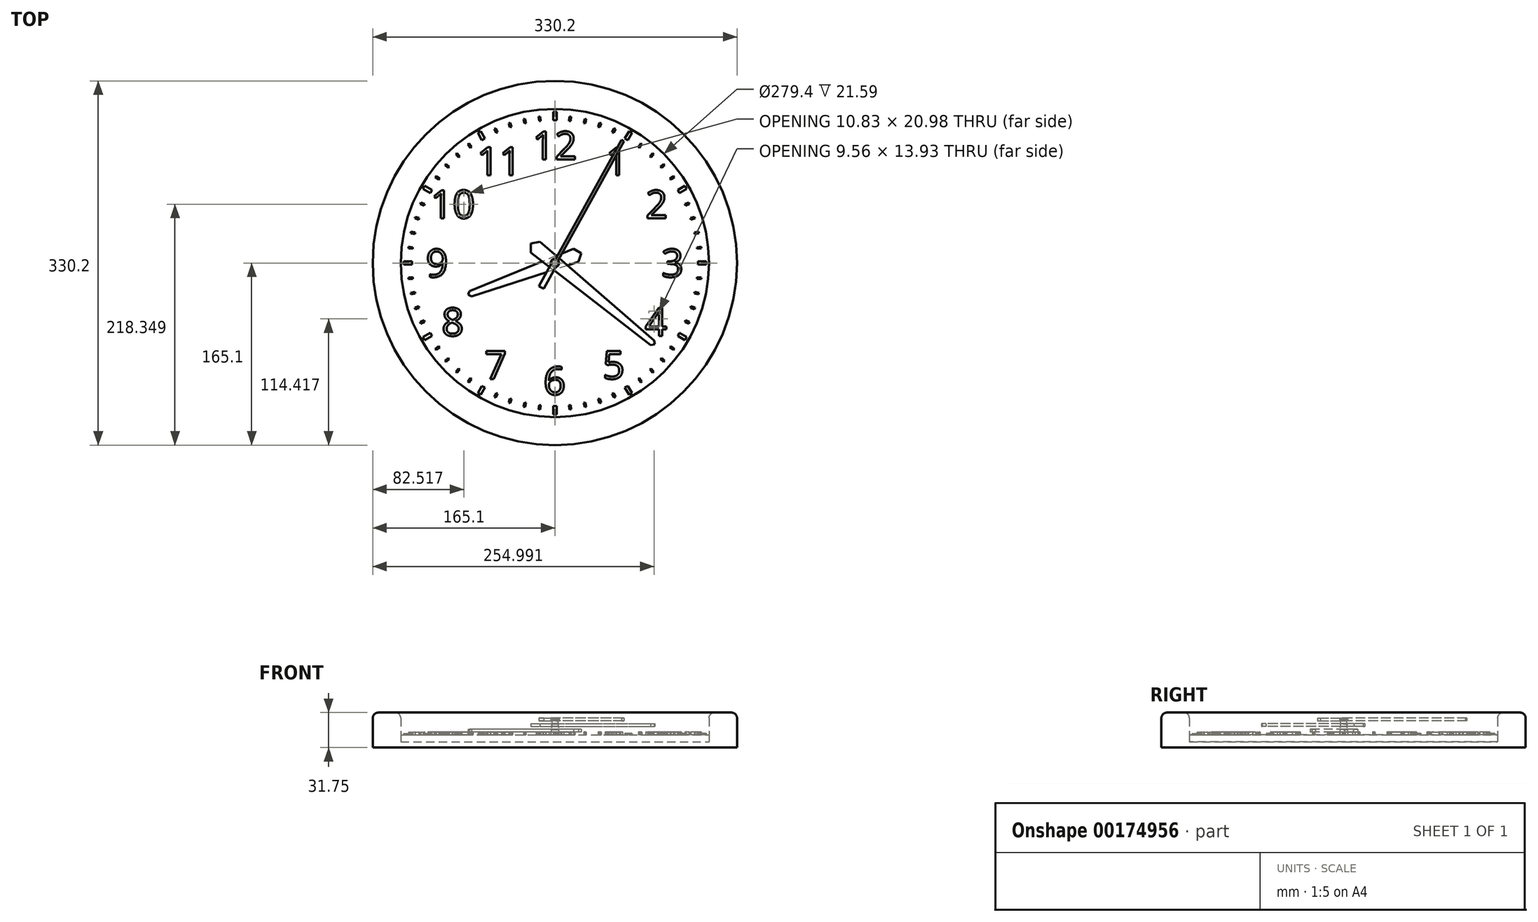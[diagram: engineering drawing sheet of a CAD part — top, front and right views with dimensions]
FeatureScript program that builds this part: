
annotation { "Feature Type Name" : "Feature", "Feature Type Description" : "" }
export const myFeature = defineFeature(function(context is Context, id is Id, definition is map)
    precondition{}
    {
        {
            var Q0;
            Q0=qCreatedBy(makeId("Front.planeOp"),FACE);
            var sketch = newSketch(context, id + "F0", { "sketchPlane" : qUnion([Q0])});
            skLineSegment(sketch, "E0", {"start": v(0, 0) * mm, "end": v(0, 54.8) * mm, "construction": true});
            skLineSegment(sketch, "E1.bottom", {"start": v(139.7, 0) * mm, "end": v(165.1, 0) * mm});
            skLineSegment(sketch, "E1.top", {"start": v(139.7, 31.75) * mm, "end": v(165.1, 31.75) * mm});
            skLineSegment(sketch, "E1.left", {"start": v(139.7, 5.08) * mm, "end": v(139.7, 31.75) * mm});
            skLineSegment(sketch, "E1.right", {"start": v(165.1, 0) * mm, "end": v(165.1, 31.75) * mm});
            skLineSegment(sketch, "E2", {"start": v(152.4, 0) * mm, "end": v(152.4, 31.75) * mm, "construction": true});
            skLineSegment(sketch, "E3.bottom", {"start": v(0, 0) * mm, "end": v(139.7, 0) * mm});
            skLineSegment(sketch, "E3.top", {"start": v(0, 5.08) * mm, "end": v(139.7, 5.08) * mm});
            skLineSegment(sketch, "E3.left", {"start": v(0, 0) * mm, "end": v(0, 5.08) * mm});
            skSolve(sketch);
        }
        {
            var Q0;
            Q0=makeQuery(id+"F0.imprint","IMPRINT",FACE,{"disambiguationData":[TD([[makeQuery(id+"F0.imprint","IMPRINT",EDGE,{"derivedFrom":sQuery(id+"F0.wireOp",EDGE,"E1.bottom")}),1.0]])]});
            var Q1;
            Q1=sQuery(id+"F0.wireOp",EDGE,"E0");
            revolve(context, id + "F1", {"entities" : qUnion([Q0]), "axis" : qUnion([Q1]), "revolveType" : RevolveType.FULL});
        }
        {
            var Q0;
            Q0=makeQuery(id+"F1.opRevolve","SWEPT_EDGE",EDGE,{"disambiguationData":[OSD([sQuery(id+"F0.wireOp",EDGE,"E1.top"),sQuery(id+"F0.wireOp",EDGE,"E1.left")])]});
            var Q1;
            Q1=makeQuery(id+"F1.opRevolve","SWEPT_EDGE",EDGE,{"disambiguationData":[OSD([sQuery(id+"F0.wireOp",EDGE,"E1.top"),sQuery(id+"F0.wireOp",EDGE,"E1.right")])]});
            fillet(context, id + "F2", {"entities" : qUnion([Q0, Q1]), "radius" : 5.08 * mm, "tangentPropagation" : true, "allowEdgeOverflow" : false});
        }
        {
            var Q0;
            Q0=makeQuery(id+"F1.opRevolve","SWEPT_FACE",FACE,{"disambiguationData":[OSD([sQuery(id+"F0.wireOp",EDGE,"E3.top")])]});
            extrude(context, id + "F3", {"entities" : qUnion([Q0]), "depth" : 6.35 * mm});
        }
        {
            var Q0;
            Q0=makeQuery(id+"F3.opExtrude","CAP_FACE",FACE,{"disambiguationData":[OSD([sQuery(id+"F0.wireOp",EDGE,"E3.top")])],"isStart":false});
            var sketch = newSketch(context, id + "F4", { "sketchPlane" : qUnion([Q0])});
            skText(sketch, "E4", { "text": "12", "fontName": "OpenSans-Regular.ttf"});
            skLineSegment(sketch, "E5", {"start": v(0, 0) * mm, "end": v(0, 106.68) * mm, "construction": true});
            skLineSegment(sketch, "E6.1.0", {"start": v(0, 0) * mm, "end": v(-53.34, 92.39) * mm, "construction": true});
            skLineSegment(sketch, "E6.2.0", {"start": v(0, 0) * mm, "end": v(-92.39, 53.34) * mm, "construction": true});
            skLineSegment(sketch, "E6.3.0", {"start": v(0, 0) * mm, "end": v(-106.68, 0) * mm, "construction": true});
            skLineSegment(sketch, "E6.4.0", {"start": v(0, 0) * mm, "end": v(-92.39, -53.34) * mm, "construction": true});
            skLineSegment(sketch, "E6.5.0", {"start": v(0, 0) * mm, "end": v(-53.34, -92.39) * mm, "construction": true});
            skLineSegment(sketch, "E6.6.0", {"start": v(0, 0) * mm, "end": v(0, -106.68) * mm, "construction": true});
            skLineSegment(sketch, "E6.7.0", {"start": v(0, 0) * mm, "end": v(53.34, -92.39) * mm, "construction": true});
            skLineSegment(sketch, "E6.8.0", {"start": v(0, 0) * mm, "end": v(92.39, -53.34) * mm, "construction": true});
            skLineSegment(sketch, "E6.9.0", {"start": v(0, 0) * mm, "end": v(106.68, 0) * mm, "construction": true});
            skLineSegment(sketch, "E6.10.0", {"start": v(0, 0) * mm, "end": v(92.39, 53.34) * mm, "construction": true});
            skLineSegment(sketch, "E6.11.0", {"start": v(0, 0) * mm, "end": v(53.34, 92.39) * mm, "construction": true});
            skPoint(sketch, "E6.center", {"position": v(0, 0) * mm});
            skText(sketch, "E7", { "text": "2", "fontName": "OpenSans-Regular.ttf"});
            skText(sketch, "E8", { "text": "3", "fontName": "OpenSans-Regular.ttf"});
            skText(sketch, "E9", { "text": "4", "fontName": "OpenSans-Regular.ttf"});
            skText(sketch, "E10", { "text": "1", "fontName": "OpenSans-Regular.ttf"});
            skText(sketch, "E11", { "text": "5", "fontName": "OpenSans-Regular.ttf"});
            skText(sketch, "E12", { "text": "6", "fontName": "OpenSans-Regular.ttf"});
            skText(sketch, "E13", { "text": "7", "fontName": "OpenSans-Regular.ttf"});
            skText(sketch, "E14", { "text": "9", "fontName": "OpenSans-Regular.ttf"});
            skText(sketch, "E15", { "text": "8", "fontName": "OpenSans-Regular.ttf"});
            skText(sketch, "E16", { "text": "10", "fontName": "OpenSans-Regular.ttf"});
            skText(sketch, "E17", { "text": "11", "fontName": "OpenSans-Regular.ttf"});
            const initialGuessF4  = {"E4": [-0.02037, 0.09398, 1, 0, 0.0254], "E7": [0.0821, 0.04064, 1, 0, 0.0254], "E8": [0.09649, -0.0127, 1, 0, 0.0254], "E9": [0.08151, -0.06604, 1, 0, 0.0254], "E10": [0.04604, 0.07969, 1, 0, 0.0254], "E11": [0.04313, -0.10509, 1, 0, 0.0254], "E12": [-0.01037, -0.11938, 1, 0, 0.0254], "E13": [-0.06367, -0.10509, 1, 0, 0.0254], "E14": [-0.11696, -0.0127, 1, 0, 0.0254], "E15": [-0.1027, -0.06604, 1, 0, 0.0254], "E16": [-0.11282, 0.04064, 1, 0, 0.0254], "E17": [-0.07073, 0.07969, 1, 0, 0.0254]};
            skSetInitialGuess(sketch, initialGuessF4);
            skSolve(sketch);
        }
        {
            var Q0;
            Q0 = qSketchRegion(id + "F4", true);
            extrude(context, id + "F5", {"entities" : qUnion([Q0]), "depth" : 2.54 * mm});
        }
        {
            var Q0;
            Q0=makeQuery(id+"F3.opExtrude","CAP_FACE",FACE,{"disambiguationData":[OSD([sQuery(id+"F0.wireOp",EDGE,"E3.top")])],"isStart":false});
            var sketch = newSketch(context, id + "F6", { "sketchPlane" : qUnion([Q0])});
            skCircle(sketch, "E18", {"center": v(0, 0) * mm, "radius": 3.81 * mm});
            skSolve(sketch);
        }
        {
            var Q0;
            Q0=makeQuery(id+"F6.imprint","IMPRINT",FACE,{"disambiguationData":[TD([[makeQuery(id+"F6.imprint","IMPRINT",EDGE,{"derivedFrom":sQuery(id+"F6.wireOp",EDGE,"E18")}),-1.0]])]});
            cPlane(context, id + "F7", {"entities" : qUnion([Q0]), "cplaneType" : CPlaneType.OFFSET, "offset" : 13.97 * mm, "width" : 152.4 * mm, "height" : 152.4 * mm});
        }
        {
            var Q0;
            Q0=qCreatedBy(id+"F7.planeOp",FACE);
            var sketch = newSketch(context, id + "F8", { "sketchPlane" : qUnion([Q0])});
            skCircle(sketch, "E19", {"center": v(0, 0) * mm, "radius": 2.54 * mm});
            skSolve(sketch);
        }
        {
            var Q1;
            Q1=makeQuery(id+"F6.imprint","IMPRINT",FACE,{"disambiguationData":[TD([[makeQuery(id+"F6.imprint","IMPRINT",EDGE,{"derivedFrom":sQuery(id+"F6.wireOp",EDGE,"E18")}),1.0]])]});
            var Q2;
            Q2=makeQuery(id+"F8.imprint","IMPRINT",FACE,{"disambiguationData":[TD([[makeQuery(id+"F8.imprint","IMPRINT",EDGE,{"derivedFrom":sQuery(id+"F8.wireOp",EDGE,"E19")}),1.0]])]});
            loft(context, id + "F9", {"sheetProfilesArray" : [{ "sheetProfileEntities" : qUnion([Q1]) }, { "sheetProfileEntities" : qUnion([Q2]) }]});
        }
        {
            var Q0;
            Q0=makeQuery(id+"F3.opExtrude","CAP_FACE",FACE,{"disambiguationData":[OSD([sQuery(id+"F0.wireOp",EDGE,"E3.top")])],"isStart":false});
            cPlane(context, id + "F10", {"entities" : qUnion([Q0]), "cplaneType" : CPlaneType.OFFSET, "offset" : 2.54 * mm, "width" : 152.4 * mm, "height" : 152.4 * mm});
        }
        {
            var Q0;
            Q0=qCreatedBy(id+"F10.planeOp",FACE);
            var sketch = newSketch(context, id + "F11", { "sketchPlane" : qUnion([Q0])});
            skLineSegment(sketch, "E20", {"start": v(-4.77, -1.74) * mm, "end": v(-76.38, -27.8) * mm, "construction": true});
            skLineSegment(sketch, "E21", {"start": v(-76.38, -27.8) * mm, "end": v(-77.25, -25.41) * mm, "construction": true});
            skLineSegment(sketch, "E22", {"start": v(19.1, 6.95) * mm, "end": v(16.92, 12.92) * mm, "construction": true});
            skLineSegment(sketch, "E23", {"start": v(-4.77, -1.74) * mm, "end": v(23.87, 8.69) * mm, "construction": true});
            skLineSegment(sketch, "E24", {"start": v(23.87, 8.69) * mm, "end": v(16.92, 12.92) * mm});
            skLineSegment(sketch, "E25", {"start": v(16.92, 12.92) * mm, "end": v(-77.25, -25.41) * mm});
            skLineSegment(sketch, "E26", {"start": v(-76.38, -27.8) * mm, "end": v(-78.77, -28.67) * mm, "construction": true});
            skLineSegment(sketch, "E27", {"start": v(-78.77, -28.67) * mm, "end": v(-77.25, -25.41) * mm});
            skLineSegment(sketch, "E28.MirrorCS", {"start": v(-78.77, -28.67) * mm, "end": v(-75.5, -30.19) * mm});
            skLineSegment(sketch, "E29.MirrorCS", {"start": v(21.27, 0.98) * mm, "end": v(-75.5, -30.19) * mm});
            skLineSegment(sketch, "E30.MirrorCS", {"start": v(23.87, 8.69) * mm, "end": v(21.27, 0.98) * mm});
            skSolve(sketch);
        }
        {
            var Q0;
            Q0=makeQuery(id+"F11.imprint","IMPRINT",FACE,{"disambiguationData":[TD([[makeQuery(id+"F11.imprint","IMPRINT",EDGE,{"derivedFrom":sQuery(id+"F11.wireOp",EDGE,"E24")}),1.0]])]});
            var Q1;
            Q1=makeQuery(id+"F11.imprint","IMPRINT",FACE,{"disambiguationData":[TD([[makeQuery(id+"F11.imprint","IMPRINT",EDGE,{"derivedFrom":makeQuery(id+"F9.opLoft","MID_CAP_EDGE",EDGE,{"disambiguationData":[OSD([sQuery(id+"F6.wireOp",EDGE,"E18")])],"capPos":0.0})}),1.0]])]});
            extrude(context, id + "F12", {"entities" : qUnion([Q0, Q1]), "depth" : 2.54 * mm});
        }
        {
            var Q0;
            Q0=makeQuery(id+"F12.opExtrude","CAP_FACE",FACE,{"disambiguationData":[OSD([sQuery(id+"F11.wireOp",EDGE,"E24"),sQuery(id+"F11.wireOp",EDGE,"E25"),sQuery(id+"F11.wireOp",EDGE,"E27"),sQuery(id+"F11.wireOp",EDGE,"E28.MirrorCS"),sQuery(id+"F11.wireOp",EDGE,"E29.MirrorCS"),sQuery(id+"F11.wireOp",EDGE,"E30.MirrorCS")])],"isStart":false});
            cPlane(context, id + "F13", {"entities" : qUnion([Q0]), "cplaneType" : CPlaneType.OFFSET, "offset" : 2.54 * mm, "width" : 152.4 * mm, "height" : 152.4 * mm});
        }
        {
            var Q0;
            Q0=qCreatedBy(id+"F13.planeOp",FACE);
            var sketch = newSketch(context, id + "F14", { "sketchPlane" : qUnion([Q0])});
            skLineSegment(sketch, "E31", {"start": v(0, 0) * mm, "end": v(90.48, -73.92) * mm, "construction": true});
            skLineSegment(sketch, "E32", {"start": v(0, 0) * mm, "end": v(-21.64, 17.68) * mm, "construction": true});
            skLineSegment(sketch, "E33", {"start": v(-17.7, 14.46) * mm, "end": v(-13.69, 19.38) * mm, "construction": true});
            skLineSegment(sketch, "E34", {"start": v(88.52, -72.31) * mm, "end": v(90.12, -70.35) * mm, "construction": true});
            skLineSegment(sketch, "E35", {"start": v(-21.64, 17.68) * mm, "end": v(-13.69, 19.38) * mm});
            skLineSegment(sketch, "E36", {"start": v(-13.69, 19.38) * mm, "end": v(90.12, -70.35) * mm});
            skLineSegment(sketch, "E37", {"start": v(90.12, -70.35) * mm, "end": v(90.48, -73.92) * mm});
            skLineSegment(sketch, "E38.MirrorCS", {"start": v(-21.64, 17.68) * mm, "end": v(-21.72, 9.55) * mm});
            skLineSegment(sketch, "E39.MirrorCS", {"start": v(-21.72, 9.55) * mm, "end": v(86.9, -74.28) * mm});
            skLineSegment(sketch, "E40.MirrorCS", {"start": v(86.9, -74.28) * mm, "end": v(90.48, -73.92) * mm});
            skSolve(sketch);
        }
        {
            var Q0;
            Q0=makeQuery(id+"F14.imprint","IMPRINT",FACE,{"disambiguationData":[TD([[makeQuery(id+"F14.imprint","IMPRINT",EDGE,{"derivedFrom":sQuery(id+"F14.wireOp",EDGE,"E35")}),-1.0]])]});
            extrude(context, id + "F15", {"entities" : qUnion([Q0]), "depth" : 2.54 * mm});
        }
        {
            var Q0;
            Q0=makeQuery(id+"F15.opExtrude","CAP_FACE",FACE,{"disambiguationData":[OSD([sQuery(id+"F14.wireOp",EDGE,"E35"),sQuery(id+"F14.wireOp",EDGE,"E36"),sQuery(id+"F14.wireOp",EDGE,"E37"),sQuery(id+"F14.wireOp",EDGE,"E38.MirrorCS"),sQuery(id+"F14.wireOp",EDGE,"E39.MirrorCS"),sQuery(id+"F14.wireOp",EDGE,"E40.MirrorCS")])],"isStart":false});
            cPlane(context, id + "F16", {"entities" : qUnion([Q0]), "cplaneType" : CPlaneType.OFFSET, "offset" : 2.54 * mm, "width" : 152.4 * mm, "height" : 152.4 * mm});
        }
        {
            var Q0;
            Q0=qCreatedBy(id+"F16.planeOp",FACE);
            var sketch = newSketch(context, id + "F17", { "sketchPlane" : qUnion([Q0])});
            skArc(sketch, "E41", {"start": v(0.85, -3.72) * mm, "mid": v(3.63, -1.17) * mm, "end": v(2.85, 2.53) * mm});
            skLineSegment(sketch, "E42", {"start": v(0, 0) * mm, "end": v(61.55, 111.09) * mm, "construction": true});
            skLineSegment(sketch, "E43", {"start": v(0, 0) * mm, "end": v(-12.31, -22.22) * mm, "construction": true});
            skLineSegment(sketch, "E44", {"start": v(-12.31, -22.22) * mm, "end": v(-10.09, -23.45) * mm});
            skLineSegment(sketch, "E45", {"start": v(-10.09, -23.45) * mm, "end": v(0.85, -3.72) * mm});
            skLineSegment(sketch, "E46", {"start": v(61.55, 111.09) * mm, "end": v(62.66, 110.47) * mm});
            skLineSegment(sketch, "E47", {"start": v(62.66, 110.47) * mm, "end": v(2.85, 2.53) * mm});
            skLineSegment(sketch, "E48.MirrorCS", {"start": v(61.55, 111.09) * mm, "end": v(60.44, 111.7) * mm});
            skLineSegment(sketch, "E49.MirrorCS", {"start": v(60.44, 111.7) * mm, "end": v(0.63, 3.76) * mm});
            skArc(sketch, "E50.MirrorCS", {"start": v(-3.6, -1.25) * mm, "mid": v(-2.91, 2.46) * mm, "end": v(0.63, 3.76) * mm});
            skLineSegment(sketch, "E51.MirrorCS", {"start": v(-14.53, -20.99) * mm, "end": v(-3.6, -1.25) * mm});
            skLineSegment(sketch, "E52.MirrorCS", {"start": v(-12.31, -22.22) * mm, "end": v(-14.53, -20.99) * mm});
            skSolve(sketch);
        }
        {
            var Q0;
            Q0=makeQuery(id+"F17.imprint","IMPRINT",FACE,{"disambiguationData":[TD([[makeQuery(id+"F17.imprint","IMPRINT",EDGE,{"derivedFrom":sQuery(id+"F17.wireOp",EDGE,"E41")}),1.0]])]});
            extrude(context, id + "F18", {"entities" : qUnion([Q0]), "depth" : 2.54 * mm});
        }
        {
            var Q0;
            Q0=makeQuery(id+"F9.opLoft","SWEPT_BODY",BODY,{"disambiguationData":[OSD([makeQuery(id+"F6.imprint","IMPRINT",FACE,{"disambiguationData":[TD([[makeQuery(id+"F6.imprint","IMPRINT",EDGE,{"derivedFrom":sQuery(id+"F6.wireOp",EDGE,"E18")}),1.0]])]}),makeQuery(id+"F8.imprint","IMPRINT",FACE,{"disambiguationData":[TD([[makeQuery(id+"F8.imprint","IMPRINT",EDGE,{"derivedFrom":sQuery(id+"F8.wireOp",EDGE,"E19")}),1.0]])]})])]});
            var Q1;
            Q1=makeQuery(id+"F12.opExtrude","SWEPT_BODY",BODY,{"disambiguationData":[OSD([sQuery(id+"F11.wireOp",EDGE,"E24"),sQuery(id+"F11.wireOp",EDGE,"E25"),sQuery(id+"F11.wireOp",EDGE,"E27"),sQuery(id+"F11.wireOp",EDGE,"E28.MirrorCS"),sQuery(id+"F11.wireOp",EDGE,"E29.MirrorCS"),sQuery(id+"F11.wireOp",EDGE,"E30.MirrorCS")])]});
            booleanBodies(context, id + "F19", {"operationType" : BooleanOperationType.SUBTRACTION, "tools" : qUnion([Q0]), "targets" : qUnion([Q1]), "keepTools" : true});
        }
        {
            var Q0;
            Q0=makeQuery(id+"F9.opLoft","SWEPT_BODY",BODY,{"disambiguationData":[OSD([makeQuery(id+"F6.imprint","IMPRINT",FACE,{"disambiguationData":[TD([[makeQuery(id+"F6.imprint","IMPRINT",EDGE,{"derivedFrom":sQuery(id+"F6.wireOp",EDGE,"E18")}),1.0]])]}),makeQuery(id+"F8.imprint","IMPRINT",FACE,{"disambiguationData":[TD([[makeQuery(id+"F8.imprint","IMPRINT",EDGE,{"derivedFrom":sQuery(id+"F8.wireOp",EDGE,"E19")}),1.0]])]})])]});
            var Q1;
            Q1=makeQuery(id+"F15.opExtrude","SWEPT_BODY",BODY,{"disambiguationData":[OSD([sQuery(id+"F14.wireOp",EDGE,"E35"),sQuery(id+"F14.wireOp",EDGE,"E36"),sQuery(id+"F14.wireOp",EDGE,"E37"),sQuery(id+"F14.wireOp",EDGE,"E38.MirrorCS"),sQuery(id+"F14.wireOp",EDGE,"E39.MirrorCS"),sQuery(id+"F14.wireOp",EDGE,"E40.MirrorCS")])]});
            booleanBodies(context, id + "F20", {"operationType" : BooleanOperationType.SUBTRACTION, "tools" : qUnion([Q0]), "targets" : qUnion([Q1]), "keepTools" : true});
        }
        {
            var Q0;
            Q0=makeQuery(id+"F9.opLoft","SWEPT_BODY",BODY,{"disambiguationData":[OSD([makeQuery(id+"F6.imprint","IMPRINT",FACE,{"disambiguationData":[TD([[makeQuery(id+"F6.imprint","IMPRINT",EDGE,{"derivedFrom":sQuery(id+"F6.wireOp",EDGE,"E18")}),1.0]])]}),makeQuery(id+"F8.imprint","IMPRINT",FACE,{"disambiguationData":[TD([[makeQuery(id+"F8.imprint","IMPRINT",EDGE,{"derivedFrom":sQuery(id+"F8.wireOp",EDGE,"E19")}),1.0]])]})])]});
            var Q1;
            Q1=makeQuery(id+"F18.opExtrude","SWEPT_BODY",BODY,{"disambiguationData":[OSD([sQuery(id+"F17.wireOp",EDGE,"E41"),sQuery(id+"F17.wireOp",EDGE,"E44"),sQuery(id+"F17.wireOp",EDGE,"E45"),sQuery(id+"F17.wireOp",EDGE,"E46"),sQuery(id+"F17.wireOp",EDGE,"E47"),sQuery(id+"F17.wireOp",EDGE,"E48.MirrorCS"),sQuery(id+"F17.wireOp",EDGE,"E49.MirrorCS"),sQuery(id+"F17.wireOp",EDGE,"E50.MirrorCS"),sQuery(id+"F17.wireOp",EDGE,"E51.MirrorCS"),sQuery(id+"F17.wireOp",EDGE,"E52.MirrorCS")])]});
            booleanBodies(context, id + "F21", {"operationType" : BooleanOperationType.SUBTRACTION, "tools" : qUnion([Q0]), "targets" : qUnion([Q1]), "keepTools" : true});
        }
        {
            var Q0;
            Q0=makeQuery(id+"F19.opBoolean","INTERSECT",EDGE,{"derivedFrom":[makeQuery(id+"F9.opLoft","SWEPT_FACE",FACE,{"disambiguationData":[OSD([sQuery(id+"F6.wireOp",EDGE,"E18"),sQuery(id+"F8.wireOp",EDGE,"E19")])]}),makeQuery(id+"F12.opExtrude","CAP_FACE",FACE,{"disambiguationData":[OSD([sQuery(id+"F11.wireOp",EDGE,"E24"),sQuery(id+"F11.wireOp",EDGE,"E25"),sQuery(id+"F11.wireOp",EDGE,"E27"),sQuery(id+"F11.wireOp",EDGE,"E28.MirrorCS"),sQuery(id+"F11.wireOp",EDGE,"E29.MirrorCS"),sQuery(id+"F11.wireOp",EDGE,"E30.MirrorCS")])],"isStart":true})]});
            var Q1;
            Q1=makeQuery(id+"F19.opBoolean","INTERSECT",EDGE,{"derivedFrom":[makeQuery(id+"F9.opLoft","SWEPT_FACE",FACE,{"disambiguationData":[OSD([sQuery(id+"F6.wireOp",EDGE,"E18"),sQuery(id+"F8.wireOp",EDGE,"E19")])]}),makeQuery(id+"F12.opExtrude","CAP_FACE",FACE,{"disambiguationData":[OSD([sQuery(id+"F11.wireOp",EDGE,"E24"),sQuery(id+"F11.wireOp",EDGE,"E25"),sQuery(id+"F11.wireOp",EDGE,"E27"),sQuery(id+"F11.wireOp",EDGE,"E28.MirrorCS"),sQuery(id+"F11.wireOp",EDGE,"E29.MirrorCS"),sQuery(id+"F11.wireOp",EDGE,"E30.MirrorCS")])],"isStart":false})]});
            var Q2;
            Q2=makeQuery(id+"F20.opBoolean","INTERSECT",EDGE,{"derivedFrom":[makeQuery(id+"F9.opLoft","SWEPT_FACE",FACE,{"disambiguationData":[OSD([sQuery(id+"F6.wireOp",EDGE,"E18"),sQuery(id+"F8.wireOp",EDGE,"E19")])]}),makeQuery(id+"F15.opExtrude","CAP_FACE",FACE,{"disambiguationData":[OSD([sQuery(id+"F14.wireOp",EDGE,"E35"),sQuery(id+"F14.wireOp",EDGE,"E36"),sQuery(id+"F14.wireOp",EDGE,"E37"),sQuery(id+"F14.wireOp",EDGE,"E38.MirrorCS"),sQuery(id+"F14.wireOp",EDGE,"E39.MirrorCS"),sQuery(id+"F14.wireOp",EDGE,"E40.MirrorCS")])],"isStart":true})]});
            var Q3;
            Q3=makeQuery(id+"F20.opBoolean","INTERSECT",EDGE,{"derivedFrom":[makeQuery(id+"F9.opLoft","SWEPT_FACE",FACE,{"disambiguationData":[OSD([sQuery(id+"F6.wireOp",EDGE,"E18"),sQuery(id+"F8.wireOp",EDGE,"E19")])]}),makeQuery(id+"F15.opExtrude","CAP_FACE",FACE,{"disambiguationData":[OSD([sQuery(id+"F14.wireOp",EDGE,"E35"),sQuery(id+"F14.wireOp",EDGE,"E36"),sQuery(id+"F14.wireOp",EDGE,"E37"),sQuery(id+"F14.wireOp",EDGE,"E38.MirrorCS"),sQuery(id+"F14.wireOp",EDGE,"E39.MirrorCS"),sQuery(id+"F14.wireOp",EDGE,"E40.MirrorCS")])],"isStart":false})]});
            var Q4;
            Q4=makeQuery(id+"F21.opBoolean","INTERSECT",EDGE,{"derivedFrom":[makeQuery(id+"F9.opLoft","SWEPT_FACE",FACE,{"disambiguationData":[OSD([sQuery(id+"F6.wireOp",EDGE,"E18"),sQuery(id+"F8.wireOp",EDGE,"E19")])]}),makeQuery(id+"F18.opExtrude","CAP_FACE",FACE,{"disambiguationData":[OSD([sQuery(id+"F17.wireOp",EDGE,"E41"),sQuery(id+"F17.wireOp",EDGE,"E44"),sQuery(id+"F17.wireOp",EDGE,"E45"),sQuery(id+"F17.wireOp",EDGE,"E46"),sQuery(id+"F17.wireOp",EDGE,"E47"),sQuery(id+"F17.wireOp",EDGE,"E48.MirrorCS"),sQuery(id+"F17.wireOp",EDGE,"E49.MirrorCS"),sQuery(id+"F17.wireOp",EDGE,"E50.MirrorCS"),sQuery(id+"F17.wireOp",EDGE,"E51.MirrorCS"),sQuery(id+"F17.wireOp",EDGE,"E52.MirrorCS")])],"isStart":true})]});
            var Q5;
            Q5=makeQuery(id+"F21.opBoolean","COPY",EDGE,{"derivedFrom":makeQuery(id+"F9.opLoft","MID_CAP_EDGE",EDGE,{"disambiguationData":[OSD([sQuery(id+"F6.wireOp",EDGE,"E18"),sQuery(id+"F8.wireOp",EDGE,"E19")])],"capPos":1.0})});
            chamfer(context, id + "F22", {"entities" : qUnion([Q0, Q1, Q2, Q3, Q4, Q5]), "width" : 0.25 * mm, "tangentPropagation" : true});
        }
        {
            var Q0;
            Q0=makeQuery(id+"F3.opExtrude","CAP_FACE",FACE,{"disambiguationData":[OSD([sQuery(id+"F0.wireOp",EDGE,"E3.top")])],"isStart":false});
            var sketch = newSketch(context, id + "F23", { "sketchPlane" : qUnion([Q0])});
            skLineSegment(sketch, "E53", {"start": v(0, 0) * mm, "end": v(0, 139.7) * mm, "construction": true});
            skLineSegment(sketch, "E54.bottom", {"start": v(1.52, 137.16) * mm, "end": v(-1.52, 137.16) * mm});
            skLineSegment(sketch, "E54.top", {"start": v(1.52, 129.54) * mm, "end": v(-1.52, 129.54) * mm});
            skLineSegment(sketch, "E54.left", {"start": v(1.52, 137.16) * mm, "end": v(1.52, 129.54) * mm});
            skLineSegment(sketch, "E54.right", {"start": v(-1.52, 137.16) * mm, "end": v(-1.52, 129.54) * mm});
            skPoint(sketch, "E54.middle", {"position": v(0, 133.35) * mm});
            skSolve(sketch);
        }
        {
            var Q0;
            Q0=makeQuery(id+"F23.imprint","IMPRINT",FACE,{"disambiguationData":[TD([[makeQuery(id+"F23.imprint","IMPRINT",EDGE,{"derivedFrom":sQuery(id+"F23.wireOp",EDGE,"E54.bottom")}),1.0]])]});
            extrude(context, id + "F24", {"entities" : qUnion([Q0]), "depth" : 1.27 * mm});
        }
        {
            var Q0;
            Q0=makeQuery(id+"F24.opExtrude","SWEPT_BODY",BODY,{"disambiguationData":[OSD([sQuery(id+"F23.wireOp",EDGE,"E54.bottom"),sQuery(id+"F23.wireOp",EDGE,"E54.top"),sQuery(id+"F23.wireOp",EDGE,"E54.left"),sQuery(id+"F23.wireOp",EDGE,"E54.right")])]});
            var Q1;
            Q1=sQuery(id+"F0.wireOp",EDGE,"E0");
            circularPattern(context, id + "F25", {"entities" : qUnion([Q0]), "axis" : qUnion([Q1]), "angle" : 360 * degree, "instanceCount" : 12, "equalSpace" : true});
        }
        {
            var Q0;
            Q0=makeQuery(id+"F3.opExtrude","CAP_FACE",FACE,{"disambiguationData":[OSD([sQuery(id+"F0.wireOp",EDGE,"E3.top")])],"isStart":false});
            var sketch = newSketch(context, id + "F26", { "sketchPlane" : qUnion([Q0])});
            skLineSegment(sketch, "E55", {"start": v(0, 0) * mm, "end": v(0, 65.46) * mm, "construction": true});
            skLineSegment(sketch, "E56", {"start": v(0, 0) * mm, "end": v(13.94, 132.62) * mm, "construction": true});
            skLineSegment(sketch, "E57", {"start": v(13.54, 128.83) * mm, "end": v(14.3, 128.75) * mm});
            skLineSegment(sketch, "E58", {"start": v(13.94, 132.62) * mm, "end": v(14.7, 132.54) * mm});
            skLineSegment(sketch, "E59", {"start": v(14.7, 132.54) * mm, "end": v(14.3, 128.75) * mm});
            skLineSegment(sketch, "E60.MirrorCS", {"start": v(13.94, 132.62) * mm, "end": v(13.18, 132.7) * mm});
            skLineSegment(sketch, "E61.MirrorCS", {"start": v(13.18, 132.7) * mm, "end": v(12.78, 128.91) * mm});
            skLineSegment(sketch, "E62.MirrorCS", {"start": v(13.54, 128.83) * mm, "end": v(12.78, 128.91) * mm});
            skLineSegment(sketch, "E63.2.0", {"start": v(-13.18, 132.7) * mm, "end": v(-12.78, 128.91) * mm});
            skLineSegment(sketch, "E63.2.1", {"start": v(-13.94, 132.62) * mm, "end": v(-13.18, 132.7) * mm});
            skLineSegment(sketch, "E63.2.2", {"start": v(-13.94, 132.62) * mm, "end": v(-14.7, 132.54) * mm});
            skLineSegment(sketch, "E63.2.3", {"start": v(-14.7, 132.54) * mm, "end": v(-14.3, 128.75) * mm});
            skLineSegment(sketch, "E63.2.4", {"start": v(-13.54, 128.83) * mm, "end": v(-14.3, 128.75) * mm});
            skLineSegment(sketch, "E63.2.5", {"start": v(-13.54, 128.83) * mm, "end": v(-12.78, 128.91) * mm});
            skLineSegment(sketch, "E63.3.0", {"start": v(-26.98, 130.6) * mm, "end": v(-26.19, 126.87) * mm});
            skLineSegment(sketch, "E63.3.1", {"start": v(-27.73, 130.44) * mm, "end": v(-26.98, 130.6) * mm});
            skLineSegment(sketch, "E63.3.2", {"start": v(-27.73, 130.44) * mm, "end": v(-28.47, 130.28) * mm});
            skLineSegment(sketch, "E63.3.3", {"start": v(-28.47, 130.28) * mm, "end": v(-27.68, 126.55) * mm});
            skLineSegment(sketch, "E63.3.4", {"start": v(-26.93, 126.7) * mm, "end": v(-27.68, 126.55) * mm});
            skLineSegment(sketch, "E63.3.5", {"start": v(-26.93, 126.7) * mm, "end": v(-26.19, 126.87) * mm});
            skLineSegment(sketch, "E63.4.0", {"start": v(-40.48, 127.06) * mm, "end": v(-39.3, 123.44) * mm});
            skLineSegment(sketch, "E63.4.1", {"start": v(-41.2, 126.82) * mm, "end": v(-40.48, 127.06) * mm});
            skLineSegment(sketch, "E63.4.2", {"start": v(-41.2, 126.82) * mm, "end": v(-41.93, 126.59) * mm});
            skLineSegment(sketch, "E63.4.3", {"start": v(-41.93, 126.59) * mm, "end": v(-40.75, 122.96) * mm});
            skLineSegment(sketch, "E63.4.4", {"start": v(-40.03, 123.2) * mm, "end": v(-40.75, 122.96) * mm});
            skLineSegment(sketch, "E63.4.5", {"start": v(-40.03, 123.2) * mm, "end": v(-39.3, 123.44) * mm});
            skLineSegment(sketch, "E63.5.0", {"start": v(-53.54, 122.13) * mm, "end": v(-52, 118.65) * mm});
            skLineSegment(sketch, "E63.5.1", {"start": v(-54.24, 121.82) * mm, "end": v(-53.54, 122.13) * mm});
            skLineSegment(sketch, "E63.5.2", {"start": v(-54.24, 121.82) * mm, "end": v(-54.93, 121.51) * mm});
            skLineSegment(sketch, "E63.5.3", {"start": v(-54.93, 121.51) * mm, "end": v(-53.38, 118.03) * mm});
            skLineSegment(sketch, "E63.5.4", {"start": v(-52.69, 118.34) * mm, "end": v(-53.38, 118.03) * mm});
            skLineSegment(sketch, "E63.5.5", {"start": v(-52.69, 118.34) * mm, "end": v(-52, 118.65) * mm});
            skLineSegment(sketch, "E63.7.0", {"start": v(-77.76, 108.33) * mm, "end": v(-75.53, 105.25) * mm});
            skLineSegment(sketch, "E63.7.1", {"start": v(-78.38, 107.88) * mm, "end": v(-77.76, 108.33) * mm});
            skLineSegment(sketch, "E63.7.2", {"start": v(-78.38, 107.88) * mm, "end": v(-79, 107.43) * mm});
            skLineSegment(sketch, "E63.7.3", {"start": v(-79, 107.43) * mm, "end": v(-76.76, 104.35) * mm});
            skLineSegment(sketch, "E63.7.4", {"start": v(-76.14, 104.8) * mm, "end": v(-76.76, 104.35) * mm});
            skLineSegment(sketch, "E63.7.5", {"start": v(-76.14, 104.8) * mm, "end": v(-75.53, 105.25) * mm});
            skLineSegment(sketch, "E63.8.0", {"start": v(-88.66, 99.6) * mm, "end": v(-86.11, 96.78) * mm});
            skLineSegment(sketch, "E63.8.1", {"start": v(-89.23, 99.1) * mm, "end": v(-88.66, 99.6) * mm});
            skLineSegment(sketch, "E63.8.2", {"start": v(-89.23, 99.1) * mm, "end": v(-89.8, 98.59) * mm});
            skLineSegment(sketch, "E63.8.3", {"start": v(-89.8, 98.59) * mm, "end": v(-87.25, 95.76) * mm});
            skLineSegment(sketch, "E63.8.4", {"start": v(-86.68, 96.27) * mm, "end": v(-87.25, 95.76) * mm});
            skLineSegment(sketch, "E63.8.5", {"start": v(-86.68, 96.27) * mm, "end": v(-86.11, 96.78) * mm});
            skLineSegment(sketch, "E63.9.0", {"start": v(-98.59, 89.8) * mm, "end": v(-95.76, 87.25) * mm});
            skLineSegment(sketch, "E63.9.1", {"start": v(-99.1, 89.23) * mm, "end": v(-98.59, 89.8) * mm});
            skLineSegment(sketch, "E63.9.2", {"start": v(-99.1, 89.23) * mm, "end": v(-99.6, 88.66) * mm});
            skLineSegment(sketch, "E63.9.3", {"start": v(-99.6, 88.66) * mm, "end": v(-96.78, 86.11) * mm});
            skLineSegment(sketch, "E63.9.4", {"start": v(-96.27, 86.68) * mm, "end": v(-96.78, 86.11) * mm});
            skLineSegment(sketch, "E63.9.5", {"start": v(-96.27, 86.68) * mm, "end": v(-95.76, 87.25) * mm});
            skLineSegment(sketch, "E63.10.0", {"start": v(-107.43, 79) * mm, "end": v(-104.35, 76.76) * mm});
            skLineSegment(sketch, "E63.10.1", {"start": v(-107.88, 78.38) * mm, "end": v(-107.43, 79) * mm});
            skLineSegment(sketch, "E63.10.2", {"start": v(-107.88, 78.38) * mm, "end": v(-108.33, 77.76) * mm});
            skLineSegment(sketch, "E63.10.3", {"start": v(-108.33, 77.76) * mm, "end": v(-105.25, 75.53) * mm});
            skLineSegment(sketch, "E63.10.4", {"start": v(-104.8, 76.14) * mm, "end": v(-105.25, 75.53) * mm});
            skLineSegment(sketch, "E63.10.5", {"start": v(-104.8, 76.14) * mm, "end": v(-104.35, 76.76) * mm});
            skLineSegment(sketch, "E63.12.0", {"start": v(-121.51, 54.93) * mm, "end": v(-118.03, 53.38) * mm});
            skLineSegment(sketch, "E63.12.1", {"start": v(-121.82, 54.24) * mm, "end": v(-121.51, 54.93) * mm});
            skLineSegment(sketch, "E63.12.2", {"start": v(-121.82, 54.24) * mm, "end": v(-122.13, 53.54) * mm});
            skLineSegment(sketch, "E63.12.3", {"start": v(-122.13, 53.54) * mm, "end": v(-118.65, 52) * mm});
            skLineSegment(sketch, "E63.12.4", {"start": v(-118.34, 52.69) * mm, "end": v(-118.65, 52) * mm});
            skLineSegment(sketch, "E63.12.5", {"start": v(-118.34, 52.69) * mm, "end": v(-118.03, 53.38) * mm});
            skLineSegment(sketch, "E63.13.0", {"start": v(-126.59, 41.93) * mm, "end": v(-122.96, 40.75) * mm});
            skLineSegment(sketch, "E63.13.1", {"start": v(-126.82, 41.2) * mm, "end": v(-126.59, 41.93) * mm});
            skLineSegment(sketch, "E63.13.2", {"start": v(-126.82, 41.2) * mm, "end": v(-127.06, 40.48) * mm});
            skLineSegment(sketch, "E63.13.3", {"start": v(-127.06, 40.48) * mm, "end": v(-123.44, 39.3) * mm});
            skLineSegment(sketch, "E63.13.4", {"start": v(-123.2, 40.03) * mm, "end": v(-123.44, 39.3) * mm});
            skLineSegment(sketch, "E63.13.5", {"start": v(-123.2, 40.03) * mm, "end": v(-122.96, 40.75) * mm});
            skLineSegment(sketch, "E63.14.0", {"start": v(-130.28, 28.47) * mm, "end": v(-126.55, 27.68) * mm});
            skLineSegment(sketch, "E63.14.1", {"start": v(-130.44, 27.73) * mm, "end": v(-130.28, 28.47) * mm});
            skLineSegment(sketch, "E63.14.2", {"start": v(-130.44, 27.73) * mm, "end": v(-130.6, 26.98) * mm});
            skLineSegment(sketch, "E63.14.3", {"start": v(-130.6, 26.98) * mm, "end": v(-126.87, 26.19) * mm});
            skLineSegment(sketch, "E63.14.4", {"start": v(-126.7, 26.93) * mm, "end": v(-126.87, 26.19) * mm});
            skLineSegment(sketch, "E63.14.5", {"start": v(-126.7, 26.93) * mm, "end": v(-126.55, 27.68) * mm});
            skLineSegment(sketch, "E63.15.0", {"start": v(-132.54, 14.7) * mm, "end": v(-128.75, 14.3) * mm});
            skLineSegment(sketch, "E63.15.1", {"start": v(-132.62, 13.94) * mm, "end": v(-132.54, 14.7) * mm});
            skLineSegment(sketch, "E63.15.2", {"start": v(-132.62, 13.94) * mm, "end": v(-132.7, 13.18) * mm});
            skLineSegment(sketch, "E63.15.3", {"start": v(-132.7, 13.18) * mm, "end": v(-128.91, 12.78) * mm});
            skLineSegment(sketch, "E63.15.4", {"start": v(-128.83, 13.54) * mm, "end": v(-128.91, 12.78) * mm});
            skLineSegment(sketch, "E63.15.5", {"start": v(-128.83, 13.54) * mm, "end": v(-128.75, 14.3) * mm});
            skLineSegment(sketch, "E63.17.0", {"start": v(-132.7, -13.18) * mm, "end": v(-128.91, -12.78) * mm});
            skLineSegment(sketch, "E63.17.1", {"start": v(-132.62, -13.94) * mm, "end": v(-132.7, -13.18) * mm});
            skLineSegment(sketch, "E63.17.2", {"start": v(-132.62, -13.94) * mm, "end": v(-132.54, -14.7) * mm});
            skLineSegment(sketch, "E63.17.3", {"start": v(-132.54, -14.7) * mm, "end": v(-128.75, -14.3) * mm});
            skLineSegment(sketch, "E63.17.4", {"start": v(-128.83, -13.54) * mm, "end": v(-128.75, -14.3) * mm});
            skLineSegment(sketch, "E63.17.5", {"start": v(-128.83, -13.54) * mm, "end": v(-128.91, -12.78) * mm});
            skLineSegment(sketch, "E63.18.0", {"start": v(-130.6, -26.98) * mm, "end": v(-126.87, -26.19) * mm});
            skLineSegment(sketch, "E63.18.1", {"start": v(-130.44, -27.73) * mm, "end": v(-130.6, -26.98) * mm});
            skLineSegment(sketch, "E63.18.2", {"start": v(-130.44, -27.73) * mm, "end": v(-130.28, -28.47) * mm});
            skLineSegment(sketch, "E63.18.3", {"start": v(-130.28, -28.47) * mm, "end": v(-126.55, -27.68) * mm});
            skLineSegment(sketch, "E63.18.4", {"start": v(-126.7, -26.93) * mm, "end": v(-126.55, -27.68) * mm});
            skLineSegment(sketch, "E63.18.5", {"start": v(-126.7, -26.93) * mm, "end": v(-126.87, -26.19) * mm});
            skLineSegment(sketch, "E63.19.0", {"start": v(-127.06, -40.48) * mm, "end": v(-123.44, -39.3) * mm});
            skLineSegment(sketch, "E63.19.1", {"start": v(-126.82, -41.2) * mm, "end": v(-127.06, -40.48) * mm});
            skLineSegment(sketch, "E63.19.2", {"start": v(-126.82, -41.2) * mm, "end": v(-126.59, -41.93) * mm});
            skLineSegment(sketch, "E63.19.3", {"start": v(-126.59, -41.93) * mm, "end": v(-122.96, -40.75) * mm});
            skLineSegment(sketch, "E63.19.4", {"start": v(-123.2, -40.03) * mm, "end": v(-122.96, -40.75) * mm});
            skLineSegment(sketch, "E63.19.5", {"start": v(-123.2, -40.03) * mm, "end": v(-123.44, -39.3) * mm});
            skLineSegment(sketch, "E63.20.0", {"start": v(-122.13, -53.54) * mm, "end": v(-118.65, -52) * mm});
            skLineSegment(sketch, "E63.20.1", {"start": v(-121.82, -54.24) * mm, "end": v(-122.13, -53.54) * mm});
            skLineSegment(sketch, "E63.20.2", {"start": v(-121.82, -54.24) * mm, "end": v(-121.51, -54.93) * mm});
            skLineSegment(sketch, "E63.20.3", {"start": v(-121.51, -54.93) * mm, "end": v(-118.03, -53.38) * mm});
            skLineSegment(sketch, "E63.20.4", {"start": v(-118.34, -52.69) * mm, "end": v(-118.03, -53.38) * mm});
            skLineSegment(sketch, "E63.20.5", {"start": v(-118.34, -52.69) * mm, "end": v(-118.65, -52) * mm});
            skLineSegment(sketch, "E63.22.0", {"start": v(-108.33, -77.76) * mm, "end": v(-105.25, -75.53) * mm});
            skLineSegment(sketch, "E63.22.1", {"start": v(-107.88, -78.38) * mm, "end": v(-108.33, -77.76) * mm});
            skLineSegment(sketch, "E63.22.2", {"start": v(-107.88, -78.38) * mm, "end": v(-107.43, -79) * mm});
            skLineSegment(sketch, "E63.22.3", {"start": v(-107.43, -79) * mm, "end": v(-104.35, -76.76) * mm});
            skLineSegment(sketch, "E63.22.4", {"start": v(-104.8, -76.14) * mm, "end": v(-104.35, -76.76) * mm});
            skLineSegment(sketch, "E63.22.5", {"start": v(-104.8, -76.14) * mm, "end": v(-105.25, -75.53) * mm});
            skLineSegment(sketch, "E63.23.0", {"start": v(-99.6, -88.66) * mm, "end": v(-96.78, -86.11) * mm});
            skLineSegment(sketch, "E63.23.1", {"start": v(-99.1, -89.23) * mm, "end": v(-99.6, -88.66) * mm});
            skLineSegment(sketch, "E63.23.2", {"start": v(-99.1, -89.23) * mm, "end": v(-98.59, -89.8) * mm});
            skLineSegment(sketch, "E63.23.3", {"start": v(-98.59, -89.8) * mm, "end": v(-95.76, -87.25) * mm});
            skLineSegment(sketch, "E63.23.4", {"start": v(-96.27, -86.68) * mm, "end": v(-95.76, -87.25) * mm});
            skLineSegment(sketch, "E63.23.5", {"start": v(-96.27, -86.68) * mm, "end": v(-96.78, -86.11) * mm});
            skLineSegment(sketch, "E63.24.0", {"start": v(-89.8, -98.59) * mm, "end": v(-87.25, -95.76) * mm});
            skLineSegment(sketch, "E63.24.1", {"start": v(-89.23, -99.1) * mm, "end": v(-89.8, -98.59) * mm});
            skLineSegment(sketch, "E63.24.2", {"start": v(-89.23, -99.1) * mm, "end": v(-88.66, -99.6) * mm});
            skLineSegment(sketch, "E63.24.3", {"start": v(-88.66, -99.6) * mm, "end": v(-86.11, -96.78) * mm});
            skLineSegment(sketch, "E63.24.4", {"start": v(-86.68, -96.27) * mm, "end": v(-86.11, -96.78) * mm});
            skLineSegment(sketch, "E63.24.5", {"start": v(-86.68, -96.27) * mm, "end": v(-87.25, -95.76) * mm});
            skLineSegment(sketch, "E63.25.0", {"start": v(-79, -107.43) * mm, "end": v(-76.76, -104.35) * mm});
            skLineSegment(sketch, "E63.25.1", {"start": v(-78.38, -107.88) * mm, "end": v(-79, -107.43) * mm});
            skLineSegment(sketch, "E63.25.2", {"start": v(-78.38, -107.88) * mm, "end": v(-77.76, -108.33) * mm});
            skLineSegment(sketch, "E63.25.3", {"start": v(-77.76, -108.33) * mm, "end": v(-75.53, -105.25) * mm});
            skLineSegment(sketch, "E63.25.4", {"start": v(-76.14, -104.8) * mm, "end": v(-75.53, -105.25) * mm});
            skLineSegment(sketch, "E63.25.5", {"start": v(-76.14, -104.8) * mm, "end": v(-76.76, -104.35) * mm});
            skLineSegment(sketch, "E63.27.0", {"start": v(-54.93, -121.51) * mm, "end": v(-53.38, -118.03) * mm});
            skLineSegment(sketch, "E63.27.1", {"start": v(-54.24, -121.82) * mm, "end": v(-54.93, -121.51) * mm});
            skLineSegment(sketch, "E63.27.2", {"start": v(-54.24, -121.82) * mm, "end": v(-53.54, -122.13) * mm});
            skLineSegment(sketch, "E63.27.3", {"start": v(-53.54, -122.13) * mm, "end": v(-52, -118.65) * mm});
            skLineSegment(sketch, "E63.27.4", {"start": v(-52.69, -118.34) * mm, "end": v(-52, -118.65) * mm});
            skLineSegment(sketch, "E63.27.5", {"start": v(-52.69, -118.34) * mm, "end": v(-53.38, -118.03) * mm});
            skLineSegment(sketch, "E63.28.0", {"start": v(-41.93, -126.59) * mm, "end": v(-40.75, -122.96) * mm});
            skLineSegment(sketch, "E63.28.1", {"start": v(-41.2, -126.82) * mm, "end": v(-41.93, -126.59) * mm});
            skLineSegment(sketch, "E63.28.2", {"start": v(-41.2, -126.82) * mm, "end": v(-40.48, -127.06) * mm});
            skLineSegment(sketch, "E63.28.3", {"start": v(-40.48, -127.06) * mm, "end": v(-39.3, -123.44) * mm});
            skLineSegment(sketch, "E63.28.4", {"start": v(-40.03, -123.2) * mm, "end": v(-39.3, -123.44) * mm});
            skLineSegment(sketch, "E63.28.5", {"start": v(-40.03, -123.2) * mm, "end": v(-40.75, -122.96) * mm});
            skLineSegment(sketch, "E63.29.0", {"start": v(-28.47, -130.28) * mm, "end": v(-27.68, -126.55) * mm});
            skLineSegment(sketch, "E63.29.1", {"start": v(-27.73, -130.44) * mm, "end": v(-28.47, -130.28) * mm});
            skLineSegment(sketch, "E63.29.2", {"start": v(-27.73, -130.44) * mm, "end": v(-26.98, -130.6) * mm});
            skLineSegment(sketch, "E63.29.3", {"start": v(-26.98, -130.6) * mm, "end": v(-26.19, -126.87) * mm});
            skLineSegment(sketch, "E63.29.4", {"start": v(-26.93, -126.7) * mm, "end": v(-26.19, -126.87) * mm});
            skLineSegment(sketch, "E63.29.5", {"start": v(-26.93, -126.7) * mm, "end": v(-27.68, -126.55) * mm});
            skLineSegment(sketch, "E63.30.0", {"start": v(-14.7, -132.54) * mm, "end": v(-14.3, -128.75) * mm});
            skLineSegment(sketch, "E63.30.1", {"start": v(-13.94, -132.62) * mm, "end": v(-14.7, -132.54) * mm});
            skLineSegment(sketch, "E63.30.2", {"start": v(-13.94, -132.62) * mm, "end": v(-13.18, -132.7) * mm});
            skLineSegment(sketch, "E63.30.3", {"start": v(-13.18, -132.7) * mm, "end": v(-12.78, -128.91) * mm});
            skLineSegment(sketch, "E63.30.4", {"start": v(-13.54, -128.83) * mm, "end": v(-12.78, -128.91) * mm});
            skLineSegment(sketch, "E63.30.5", {"start": v(-13.54, -128.83) * mm, "end": v(-14.3, -128.75) * mm});
            skLineSegment(sketch, "E63.32.0", {"start": v(13.18, -132.7) * mm, "end": v(12.78, -128.91) * mm});
            skLineSegment(sketch, "E63.32.1", {"start": v(13.94, -132.62) * mm, "end": v(13.18, -132.7) * mm});
            skLineSegment(sketch, "E63.32.2", {"start": v(13.94, -132.62) * mm, "end": v(14.7, -132.54) * mm});
            skLineSegment(sketch, "E63.32.3", {"start": v(14.7, -132.54) * mm, "end": v(14.3, -128.75) * mm});
            skLineSegment(sketch, "E63.32.4", {"start": v(13.54, -128.83) * mm, "end": v(14.3, -128.75) * mm});
            skLineSegment(sketch, "E63.32.5", {"start": v(13.54, -128.83) * mm, "end": v(12.78, -128.91) * mm});
            skLineSegment(sketch, "E63.33.0", {"start": v(26.98, -130.6) * mm, "end": v(26.19, -126.87) * mm});
            skLineSegment(sketch, "E63.33.1", {"start": v(27.73, -130.44) * mm, "end": v(26.98, -130.6) * mm});
            skLineSegment(sketch, "E63.33.2", {"start": v(27.73, -130.44) * mm, "end": v(28.47, -130.28) * mm});
            skLineSegment(sketch, "E63.33.3", {"start": v(28.47, -130.28) * mm, "end": v(27.68, -126.55) * mm});
            skLineSegment(sketch, "E63.33.4", {"start": v(26.93, -126.7) * mm, "end": v(27.68, -126.55) * mm});
            skLineSegment(sketch, "E63.33.5", {"start": v(26.93, -126.7) * mm, "end": v(26.19, -126.87) * mm});
            skLineSegment(sketch, "E63.34.0", {"start": v(40.48, -127.06) * mm, "end": v(39.3, -123.44) * mm});
            skLineSegment(sketch, "E63.34.1", {"start": v(41.2, -126.82) * mm, "end": v(40.48, -127.06) * mm});
            skLineSegment(sketch, "E63.34.2", {"start": v(41.2, -126.82) * mm, "end": v(41.93, -126.59) * mm});
            skLineSegment(sketch, "E63.34.3", {"start": v(41.93, -126.59) * mm, "end": v(40.75, -122.96) * mm});
            skLineSegment(sketch, "E63.34.4", {"start": v(40.03, -123.2) * mm, "end": v(40.75, -122.96) * mm});
            skLineSegment(sketch, "E63.34.5", {"start": v(40.03, -123.2) * mm, "end": v(39.3, -123.44) * mm});
            skLineSegment(sketch, "E63.35.0", {"start": v(53.54, -122.13) * mm, "end": v(52, -118.65) * mm});
            skLineSegment(sketch, "E63.35.1", {"start": v(54.24, -121.82) * mm, "end": v(53.54, -122.13) * mm});
            skLineSegment(sketch, "E63.35.2", {"start": v(54.24, -121.82) * mm, "end": v(54.93, -121.51) * mm});
            skLineSegment(sketch, "E63.35.3", {"start": v(54.93, -121.51) * mm, "end": v(53.38, -118.03) * mm});
            skLineSegment(sketch, "E63.35.4", {"start": v(52.69, -118.34) * mm, "end": v(53.38, -118.03) * mm});
            skLineSegment(sketch, "E63.35.5", {"start": v(52.69, -118.34) * mm, "end": v(52, -118.65) * mm});
            skLineSegment(sketch, "E63.37.0", {"start": v(77.76, -108.33) * mm, "end": v(75.53, -105.25) * mm});
            skLineSegment(sketch, "E63.37.1", {"start": v(78.38, -107.88) * mm, "end": v(77.76, -108.33) * mm});
            skLineSegment(sketch, "E63.37.2", {"start": v(78.38, -107.88) * mm, "end": v(79, -107.43) * mm});
            skLineSegment(sketch, "E63.37.3", {"start": v(79, -107.43) * mm, "end": v(76.76, -104.35) * mm});
            skLineSegment(sketch, "E63.37.4", {"start": v(76.14, -104.8) * mm, "end": v(76.76, -104.35) * mm});
            skLineSegment(sketch, "E63.37.5", {"start": v(76.14, -104.8) * mm, "end": v(75.53, -105.25) * mm});
            skLineSegment(sketch, "E63.38.0", {"start": v(88.66, -99.6) * mm, "end": v(86.11, -96.78) * mm});
            skLineSegment(sketch, "E63.38.1", {"start": v(89.23, -99.1) * mm, "end": v(88.66, -99.6) * mm});
            skLineSegment(sketch, "E63.38.2", {"start": v(89.23, -99.1) * mm, "end": v(89.8, -98.59) * mm});
            skLineSegment(sketch, "E63.38.3", {"start": v(89.8, -98.59) * mm, "end": v(87.25, -95.76) * mm});
            skLineSegment(sketch, "E63.38.4", {"start": v(86.68, -96.27) * mm, "end": v(87.25, -95.76) * mm});
            skLineSegment(sketch, "E63.38.5", {"start": v(86.68, -96.27) * mm, "end": v(86.11, -96.78) * mm});
            skLineSegment(sketch, "E63.39.0", {"start": v(98.59, -89.8) * mm, "end": v(95.76, -87.25) * mm});
            skLineSegment(sketch, "E63.39.1", {"start": v(99.1, -89.23) * mm, "end": v(98.59, -89.8) * mm});
            skLineSegment(sketch, "E63.39.2", {"start": v(99.1, -89.23) * mm, "end": v(99.6, -88.66) * mm});
            skLineSegment(sketch, "E63.39.3", {"start": v(99.6, -88.66) * mm, "end": v(96.78, -86.11) * mm});
            skLineSegment(sketch, "E63.39.4", {"start": v(96.27, -86.68) * mm, "end": v(96.78, -86.11) * mm});
            skLineSegment(sketch, "E63.39.5", {"start": v(96.27, -86.68) * mm, "end": v(95.76, -87.25) * mm});
            skLineSegment(sketch, "E63.40.0", {"start": v(107.43, -79) * mm, "end": v(104.35, -76.76) * mm});
            skLineSegment(sketch, "E63.40.1", {"start": v(107.88, -78.38) * mm, "end": v(107.43, -79) * mm});
            skLineSegment(sketch, "E63.40.2", {"start": v(107.88, -78.38) * mm, "end": v(108.33, -77.76) * mm});
            skLineSegment(sketch, "E63.40.3", {"start": v(108.33, -77.76) * mm, "end": v(105.25, -75.53) * mm});
            skLineSegment(sketch, "E63.40.4", {"start": v(104.8, -76.14) * mm, "end": v(105.25, -75.53) * mm});
            skLineSegment(sketch, "E63.40.5", {"start": v(104.8, -76.14) * mm, "end": v(104.35, -76.76) * mm});
            skLineSegment(sketch, "E63.42.0", {"start": v(121.51, -54.93) * mm, "end": v(118.03, -53.38) * mm});
            skLineSegment(sketch, "E63.42.1", {"start": v(121.82, -54.24) * mm, "end": v(121.51, -54.93) * mm});
            skLineSegment(sketch, "E63.42.2", {"start": v(121.82, -54.24) * mm, "end": v(122.13, -53.54) * mm});
            skLineSegment(sketch, "E63.42.3", {"start": v(122.13, -53.54) * mm, "end": v(118.65, -52) * mm});
            skLineSegment(sketch, "E63.42.4", {"start": v(118.34, -52.69) * mm, "end": v(118.65, -52) * mm});
            skLineSegment(sketch, "E63.42.5", {"start": v(118.34, -52.69) * mm, "end": v(118.03, -53.38) * mm});
            skLineSegment(sketch, "E63.43.0", {"start": v(126.59, -41.93) * mm, "end": v(122.96, -40.75) * mm});
            skLineSegment(sketch, "E63.43.1", {"start": v(126.82, -41.2) * mm, "end": v(126.59, -41.93) * mm});
            skLineSegment(sketch, "E63.43.2", {"start": v(126.82, -41.2) * mm, "end": v(127.06, -40.48) * mm});
            skLineSegment(sketch, "E63.43.3", {"start": v(127.06, -40.48) * mm, "end": v(123.44, -39.3) * mm});
            skLineSegment(sketch, "E63.43.4", {"start": v(123.2, -40.03) * mm, "end": v(123.44, -39.3) * mm});
            skLineSegment(sketch, "E63.43.5", {"start": v(123.2, -40.03) * mm, "end": v(122.96, -40.75) * mm});
            skLineSegment(sketch, "E63.44.0", {"start": v(130.28, -28.47) * mm, "end": v(126.55, -27.68) * mm});
            skLineSegment(sketch, "E63.44.1", {"start": v(130.44, -27.73) * mm, "end": v(130.28, -28.47) * mm});
            skLineSegment(sketch, "E63.44.2", {"start": v(130.44, -27.73) * mm, "end": v(130.6, -26.98) * mm});
            skLineSegment(sketch, "E63.44.3", {"start": v(130.6, -26.98) * mm, "end": v(126.87, -26.19) * mm});
            skLineSegment(sketch, "E63.44.4", {"start": v(126.7, -26.93) * mm, "end": v(126.87, -26.19) * mm});
            skLineSegment(sketch, "E63.44.5", {"start": v(126.7, -26.93) * mm, "end": v(126.55, -27.68) * mm});
            skLineSegment(sketch, "E63.45.0", {"start": v(132.54, -14.7) * mm, "end": v(128.75, -14.3) * mm});
            skLineSegment(sketch, "E63.45.1", {"start": v(132.62, -13.94) * mm, "end": v(132.54, -14.7) * mm});
            skLineSegment(sketch, "E63.45.2", {"start": v(132.62, -13.94) * mm, "end": v(132.7, -13.18) * mm});
            skLineSegment(sketch, "E63.45.3", {"start": v(132.7, -13.18) * mm, "end": v(128.91, -12.78) * mm});
            skLineSegment(sketch, "E63.45.4", {"start": v(128.83, -13.54) * mm, "end": v(128.91, -12.78) * mm});
            skLineSegment(sketch, "E63.45.5", {"start": v(128.83, -13.54) * mm, "end": v(128.75, -14.3) * mm});
            skLineSegment(sketch, "E63.47.0", {"start": v(132.7, 13.18) * mm, "end": v(128.91, 12.78) * mm});
            skLineSegment(sketch, "E63.47.1", {"start": v(132.62, 13.94) * mm, "end": v(132.7, 13.18) * mm});
            skLineSegment(sketch, "E63.47.2", {"start": v(132.62, 13.94) * mm, "end": v(132.54, 14.7) * mm});
            skLineSegment(sketch, "E63.47.3", {"start": v(132.54, 14.7) * mm, "end": v(128.75, 14.3) * mm});
            skLineSegment(sketch, "E63.47.4", {"start": v(128.83, 13.54) * mm, "end": v(128.75, 14.3) * mm});
            skLineSegment(sketch, "E63.47.5", {"start": v(128.83, 13.54) * mm, "end": v(128.91, 12.78) * mm});
            skLineSegment(sketch, "E63.48.0", {"start": v(130.6, 26.98) * mm, "end": v(126.87, 26.19) * mm});
            skLineSegment(sketch, "E63.48.1", {"start": v(130.44, 27.73) * mm, "end": v(130.6, 26.98) * mm});
            skLineSegment(sketch, "E63.48.2", {"start": v(130.44, 27.73) * mm, "end": v(130.28, 28.47) * mm});
            skLineSegment(sketch, "E63.48.3", {"start": v(130.28, 28.47) * mm, "end": v(126.55, 27.68) * mm});
            skLineSegment(sketch, "E63.48.4", {"start": v(126.7, 26.93) * mm, "end": v(126.55, 27.68) * mm});
            skLineSegment(sketch, "E63.48.5", {"start": v(126.7, 26.93) * mm, "end": v(126.87, 26.19) * mm});
            skLineSegment(sketch, "E63.49.0", {"start": v(127.06, 40.48) * mm, "end": v(123.44, 39.3) * mm});
            skLineSegment(sketch, "E63.49.1", {"start": v(126.82, 41.2) * mm, "end": v(127.06, 40.48) * mm});
            skLineSegment(sketch, "E63.49.2", {"start": v(126.82, 41.2) * mm, "end": v(126.59, 41.93) * mm});
            skLineSegment(sketch, "E63.49.3", {"start": v(126.59, 41.93) * mm, "end": v(122.96, 40.75) * mm});
            skLineSegment(sketch, "E63.49.4", {"start": v(123.2, 40.03) * mm, "end": v(122.96, 40.75) * mm});
            skLineSegment(sketch, "E63.49.5", {"start": v(123.2, 40.03) * mm, "end": v(123.44, 39.3) * mm});
            skLineSegment(sketch, "E63.50.0", {"start": v(122.13, 53.54) * mm, "end": v(118.65, 52) * mm});
            skLineSegment(sketch, "E63.50.1", {"start": v(121.82, 54.24) * mm, "end": v(122.13, 53.54) * mm});
            skLineSegment(sketch, "E63.50.2", {"start": v(121.82, 54.24) * mm, "end": v(121.51, 54.93) * mm});
            skLineSegment(sketch, "E63.50.3", {"start": v(121.51, 54.93) * mm, "end": v(118.03, 53.38) * mm});
            skLineSegment(sketch, "E63.50.4", {"start": v(118.34, 52.69) * mm, "end": v(118.03, 53.38) * mm});
            skLineSegment(sketch, "E63.50.5", {"start": v(118.34, 52.69) * mm, "end": v(118.65, 52) * mm});
            skLineSegment(sketch, "E63.52.0", {"start": v(108.33, 77.76) * mm, "end": v(105.25, 75.53) * mm});
            skLineSegment(sketch, "E63.52.1", {"start": v(107.88, 78.38) * mm, "end": v(108.33, 77.76) * mm});
            skLineSegment(sketch, "E63.52.2", {"start": v(107.88, 78.38) * mm, "end": v(107.43, 79) * mm});
            skLineSegment(sketch, "E63.52.3", {"start": v(107.43, 79) * mm, "end": v(104.35, 76.76) * mm});
            skLineSegment(sketch, "E63.52.4", {"start": v(104.8, 76.14) * mm, "end": v(104.35, 76.76) * mm});
            skLineSegment(sketch, "E63.52.5", {"start": v(104.8, 76.14) * mm, "end": v(105.25, 75.53) * mm});
            skLineSegment(sketch, "E63.53.0", {"start": v(99.6, 88.66) * mm, "end": v(96.78, 86.11) * mm});
            skLineSegment(sketch, "E63.53.1", {"start": v(99.1, 89.23) * mm, "end": v(99.6, 88.66) * mm});
            skLineSegment(sketch, "E63.53.2", {"start": v(99.1, 89.23) * mm, "end": v(98.59, 89.8) * mm});
            skLineSegment(sketch, "E63.53.3", {"start": v(98.59, 89.8) * mm, "end": v(95.76, 87.25) * mm});
            skLineSegment(sketch, "E63.53.4", {"start": v(96.27, 86.68) * mm, "end": v(95.76, 87.25) * mm});
            skLineSegment(sketch, "E63.53.5", {"start": v(96.27, 86.68) * mm, "end": v(96.78, 86.11) * mm});
            skLineSegment(sketch, "E63.54.0", {"start": v(89.8, 98.59) * mm, "end": v(87.25, 95.76) * mm});
            skLineSegment(sketch, "E63.54.1", {"start": v(89.23, 99.1) * mm, "end": v(89.8, 98.59) * mm});
            skLineSegment(sketch, "E63.54.2", {"start": v(89.23, 99.1) * mm, "end": v(88.66, 99.6) * mm});
            skLineSegment(sketch, "E63.54.3", {"start": v(88.66, 99.6) * mm, "end": v(86.11, 96.78) * mm});
            skLineSegment(sketch, "E63.54.4", {"start": v(86.68, 96.27) * mm, "end": v(86.11, 96.78) * mm});
            skLineSegment(sketch, "E63.54.5", {"start": v(86.68, 96.27) * mm, "end": v(87.25, 95.76) * mm});
            skLineSegment(sketch, "E63.55.0", {"start": v(79, 107.43) * mm, "end": v(76.76, 104.35) * mm});
            skLineSegment(sketch, "E63.55.1", {"start": v(78.38, 107.88) * mm, "end": v(79, 107.43) * mm});
            skLineSegment(sketch, "E63.55.2", {"start": v(78.38, 107.88) * mm, "end": v(77.76, 108.33) * mm});
            skLineSegment(sketch, "E63.55.3", {"start": v(77.76, 108.33) * mm, "end": v(75.53, 105.25) * mm});
            skLineSegment(sketch, "E63.55.4", {"start": v(76.14, 104.8) * mm, "end": v(75.53, 105.25) * mm});
            skLineSegment(sketch, "E63.55.5", {"start": v(76.14, 104.8) * mm, "end": v(76.76, 104.35) * mm});
            skLineSegment(sketch, "E63.57.0", {"start": v(54.93, 121.51) * mm, "end": v(53.38, 118.03) * mm});
            skLineSegment(sketch, "E63.57.1", {"start": v(54.24, 121.82) * mm, "end": v(54.93, 121.51) * mm});
            skLineSegment(sketch, "E63.57.2", {"start": v(54.24, 121.82) * mm, "end": v(53.54, 122.13) * mm});
            skLineSegment(sketch, "E63.57.3", {"start": v(53.54, 122.13) * mm, "end": v(52, 118.65) * mm});
            skLineSegment(sketch, "E63.57.4", {"start": v(52.69, 118.34) * mm, "end": v(52, 118.65) * mm});
            skLineSegment(sketch, "E63.57.5", {"start": v(52.69, 118.34) * mm, "end": v(53.38, 118.03) * mm});
            skPoint(sketch, "E63.center", {"position": v(0, 0) * mm});
            skLineSegment(sketch, "E64.2.58.0", {"start": v(41.93, 126.59) * mm, "end": v(40.75, 122.96) * mm});
            skLineSegment(sketch, "E64.3.58.0", {"start": v(41.2, 126.82) * mm, "end": v(41.93, 126.59) * mm});
            skLineSegment(sketch, "E64.6.58.0", {"start": v(41.2, 126.82) * mm, "end": v(40.48, 127.06) * mm});
            skLineSegment(sketch, "E64.9.58.0", {"start": v(40.48, 127.06) * mm, "end": v(39.3, 123.44) * mm});
            skLineSegment(sketch, "E64.12.58.0", {"start": v(40.03, 123.2) * mm, "end": v(39.3, 123.44) * mm});
            skLineSegment(sketch, "E64.15.58.0", {"start": v(40.03, 123.2) * mm, "end": v(40.75, 122.96) * mm});
            skLineSegment(sketch, "E64.2.59.0", {"start": v(28.47, 130.28) * mm, "end": v(27.68, 126.55) * mm});
            skLineSegment(sketch, "E64.3.59.0", {"start": v(27.73, 130.44) * mm, "end": v(28.47, 130.28) * mm});
            skLineSegment(sketch, "E64.6.59.0", {"start": v(27.73, 130.44) * mm, "end": v(26.98, 130.6) * mm});
            skLineSegment(sketch, "E64.9.59.0", {"start": v(26.98, 130.6) * mm, "end": v(26.19, 126.87) * mm});
            skLineSegment(sketch, "E64.12.59.0", {"start": v(26.93, 126.7) * mm, "end": v(26.19, 126.87) * mm});
            skLineSegment(sketch, "E64.15.59.0", {"start": v(26.93, 126.7) * mm, "end": v(27.68, 126.55) * mm});
            skSolve(sketch);
        }
        {
            var Q0;
            Q0 = qSketchRegion(id + "F26", true);
            extrude(context, id + "F27", {"entities" : qUnion([Q0]), "operationType" : NewBodyOperationType.ADD, "depth" : 2.54 * mm});
        }
    });
